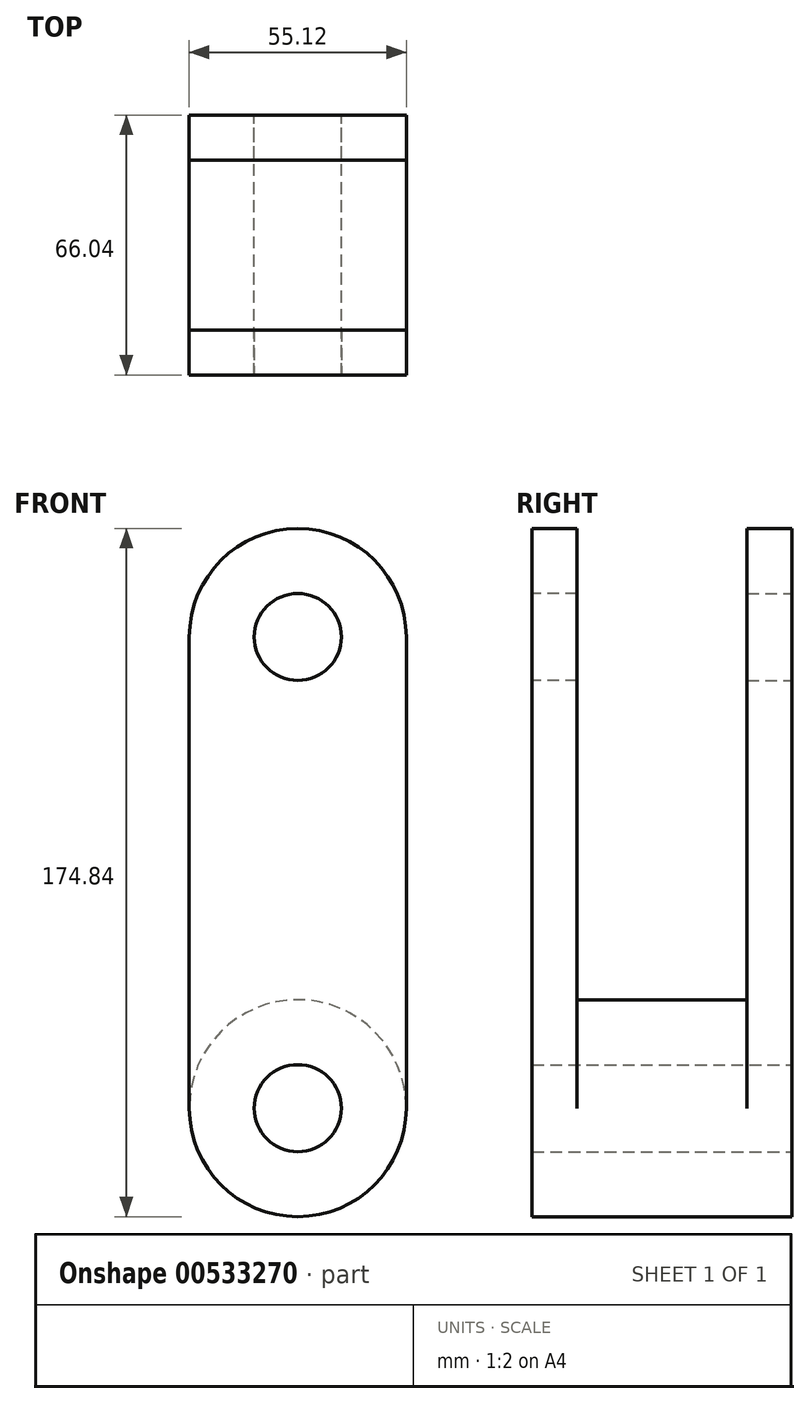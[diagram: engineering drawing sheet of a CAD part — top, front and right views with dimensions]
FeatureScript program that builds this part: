
annotation { "Feature Type Name" : "Feature", "Feature Type Description" : "" }
export const myFeature = defineFeature(function(context is Context, id is Id, definition is map)
    precondition{}
    {
        {
            var Q0;
            Q0=qCreatedBy(makeId("Front.planeOp"),FACE);
            var sketch = newSketch(context, id + "F0", { "sketchPlane" : qUnion([Q0])});
            skCircle(sketch, "E0", {"center": v(0, 0) * mm, "radius": 27.56 * mm});
            skCircle(sketch, "E1.0", {"center": v(0, 0) * mm, "radius": 11.05 * mm});
            skSolve(sketch);
        }
        {
            var Q0;
            Q0=makeQuery(id+"F0.imprint","IMPRINT",FACE,{"disambiguationData":[TD([[makeQuery(id+"F0.imprint","IMPRINT",EDGE,{"derivedFrom":sQuery(id+"F0.wireOp",EDGE,"E0")}),1.0]])]});
            extrude(context, id + "F1", {"entities" : qUnion([Q0]), "endBound" : BoundingType.SYMMETRIC, "depth" : 66.04 * mm, "offsetDistance" : 25.4 * mm});
        }
        {
            var Q0;
            Q0=makeQuery(id+"F1.opExtrude","CAP_FACE",FACE,{"disambiguationData":[OSD([sQuery(id+"F0.wireOp",EDGE,"E0"),sQuery(id+"F0.wireOp",EDGE,"E1.0")])],"isStart":false});
            var sketch = newSketch(context, id + "F2", { "sketchPlane" : qUnion([Q0])});
            skLineSegment(sketch, "E2", {"start": v(0, 0) * mm, "end": v(-27.56, 0) * mm});
            skLineSegment(sketch, "E3", {"start": v(0, 0) * mm, "end": v(27.56, 0) * mm});
            skLineSegment(sketch, "E4", {"start": v(-27.56, 0) * mm, "end": v(-27.56, 119.72) * mm});
            skLineSegment(sketch, "E5", {"start": v(27.56, 0) * mm, "end": v(27.56, 119.72) * mm});
            skLineSegment(sketch, "E6", {"start": v(-27.56, 119.72) * mm, "end": v(27.56, 119.72) * mm});
            skArc(sketch, "E7", {"start": v(27.56, 119.72) * mm, "mid": v(0, 147.28) * mm, "end": v(-27.56, 119.72) * mm});
            skArc(sketch, "E8", {"start": v(-27.56, 119.72) * mm, "mid": v(0, 92.16) * mm, "end": v(27.56, 119.72) * mm});
            skArc(sketch, "E9.0", {"start": v(11.05, 119.72) * mm, "mid": v(0, 130.77) * mm, "end": v(-11.05, 119.72) * mm});
            skArc(sketch, "E10.0", {"start": v(-11.05, 119.72) * mm, "mid": v(0, 108.67) * mm, "end": v(11.05, 119.72) * mm});
            skSolve(sketch);
        }
        {
            var Q0;
            {var subQ0=sQuery(id+"F2.wireOp",EDGE,"E4");Q0=makeQuery(id+"F2.imprint","IMPRINT",FACE,{"disambiguationData":[TD([[makeQuery(id+"F2.imprint","IMPRINT",EDGE,{"derivedFrom":subQ0}),-1.0]])]});}
            var Q1;
            {var subQ1=sQuery(id+"F2.wireOp",EDGE,"E7");Q1=makeQuery(id+"F2.imprint","IMPRINT",FACE,{"disambiguationData":[TD([[makeQuery(id+"F2.imprint","IMPRINT",EDGE,{"derivedFrom":subQ1}),1.0]])]});}
            var Q2;
            {var subQ0=sQuery(id+"F2.wireOp",EDGE,"E8");Q2=makeQuery(id+"F2.imprint","IMPRINT",FACE,{"disambiguationData":[TD([[makeQuery(id+"F2.imprint","IMPRINT",EDGE,{"derivedFrom":subQ0}),1.0]])]});}
            extrude(context, id + "F3", {"entities" : qUnion([Q0, Q1, Q2]), "operationType" : NewBodyOperationType.ADD, "oppositeDirection" : true, "depth" : 11.43 * mm, "offsetDistance" : 25.4 * mm});
        }
        {
            var Q0;
            Q0=makeQuery(id+"F1.opExtrude","CAP_FACE",FACE,{"disambiguationData":[OSD([sQuery(id+"F0.wireOp",EDGE,"E0"),sQuery(id+"F0.wireOp",EDGE,"E1.0")])],"isStart":true});
            var sketch = newSketch(context, id + "F4", { "sketchPlane" : qUnion([Q0])});
            skLineSegment(sketch, "E11", {"start": v(0, 0) * mm, "end": v(-27.56, 0) * mm});
            skLineSegment(sketch, "E12", {"start": v(0, 0) * mm, "end": v(27.56, 0) * mm});
            skLineSegment(sketch, "E13", {"start": v(27.56, 0) * mm, "end": v(27.56, 119.71) * mm});
            skLineSegment(sketch, "E14", {"start": v(-27.56, 0) * mm, "end": v(-27.56, 119.71) * mm});
            skLineSegment(sketch, "E15", {"start": v(-27.56, 119.71) * mm, "end": v(27.56, 119.71) * mm});
            skArc(sketch, "E16", {"start": v(27.56, 119.71) * mm, "mid": v(0, 147.27) * mm, "end": v(-27.56, 119.71) * mm});
            skArc(sketch, "E17", {"start": v(-27.56, 119.71) * mm, "mid": v(0, 92.15) * mm, "end": v(27.56, 119.71) * mm});
            skArc(sketch, "E18.0", {"start": v(-11.05, 119.71) * mm, "mid": v(0, 108.66) * mm, "end": v(11.05, 119.71) * mm});
            skArc(sketch, "E19.0", {"start": v(11.05, 119.71) * mm, "mid": v(0, 130.76) * mm, "end": v(-11.05, 119.71) * mm});
            skSolve(sketch);
        }
        {
            var Q0;
            {var subQ0=sQuery(id+"F4.wireOp",EDGE,"E13");Q0=makeQuery(id+"F4.imprint","IMPRINT",FACE,{"disambiguationData":[TD([[makeQuery(id+"F4.imprint","IMPRINT",EDGE,{"derivedFrom":subQ0}),1.0]])]});}
            var Q1;
            {var subQ0=sQuery(id+"F4.wireOp",EDGE,"E17");Q1=makeQuery(id+"F4.imprint","IMPRINT",FACE,{"disambiguationData":[TD([[makeQuery(id+"F4.imprint","IMPRINT",EDGE,{"derivedFrom":subQ0}),1.0]])]});}
            var Q2;
            {var subQ1=sQuery(id+"F4.wireOp",EDGE,"E16");Q2=makeQuery(id+"F4.imprint","IMPRINT",FACE,{"disambiguationData":[TD([[makeQuery(id+"F4.imprint","IMPRINT",EDGE,{"derivedFrom":subQ1}),1.0]])]});}
            extrude(context, id + "F5", {"entities" : qUnion([Q0, Q1, Q2]), "operationType" : NewBodyOperationType.ADD, "oppositeDirection" : true, "depth" : 11.43 * mm, "offsetDistance" : 25.4 * mm});
        }
    });
